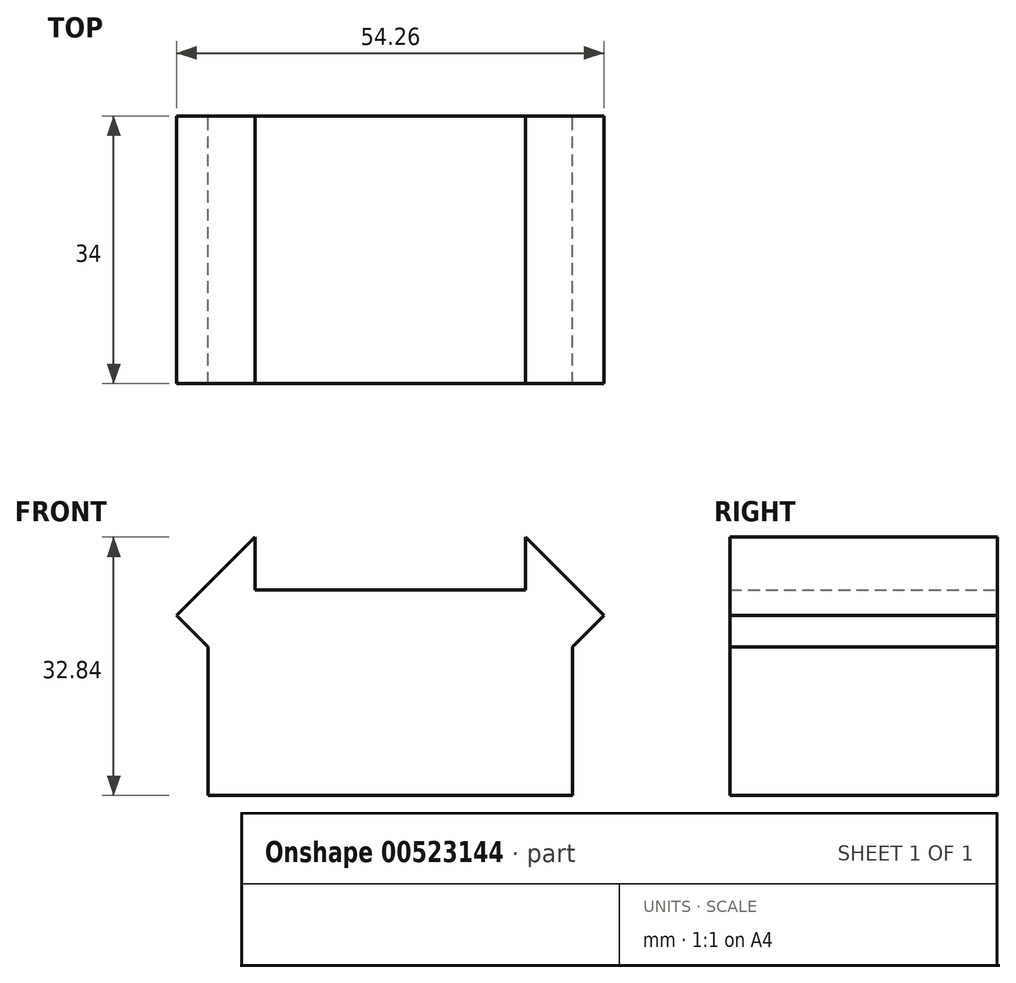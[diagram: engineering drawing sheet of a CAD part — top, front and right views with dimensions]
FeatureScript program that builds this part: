
annotation { "Feature Type Name" : "Feature", "Feature Type Description" : "" }
export const myFeature = defineFeature(function(context is Context, id is Id, definition is map)
    precondition{}
    {
        {
            var Q0;
            Q0=qCreatedBy(makeId("Front.planeOp"),FACE);
            var sketch = newSketch(context, id + "F0", { "sketchPlane" : qUnion([Q0])});
            skLineSegment(sketch, "E0", {"start": v(-23.15, -13.08) * mm, "end": v(23.15, -13.08) * mm});
            skLineSegment(sketch, "E1", {"start": v(23.15, -13.07) * mm, "end": v(23.15, 5.8) * mm});
            skLineSegment(sketch, "E2", {"start": v(23.15, 5.8) * mm, "end": v(27.13, 9.8) * mm});
            skLineSegment(sketch, "E3", {"start": v(27.13, 9.8) * mm, "end": v(17.15, 19.77) * mm});
            skLineSegment(sketch, "E4", {"start": v(17.15, 19.77) * mm, "end": v(17.15, 13.08) * mm});
            skLineSegment(sketch, "E5", {"start": v(17.15, 13.08) * mm, "end": v(-17.15, 13.07) * mm});
            skLineSegment(sketch, "E6", {"start": v(-17.15, 13.07) * mm, "end": v(-17.15, 19.77) * mm});
            skLineSegment(sketch, "E7", {"start": v(-17.15, 19.77) * mm, "end": v(-27.13, 9.8) * mm});
            skLineSegment(sketch, "E8", {"start": v(-27.13, 9.8) * mm, "end": v(-23.15, 5.8) * mm});
            skLineSegment(sketch, "E9", {"start": v(-23.15, 5.8) * mm, "end": v(-23.15, -13.08) * mm});
            skSolve(sketch);
        }
        {
            var Q0;
            Q0 = qSketchRegion(id + "F0", true);
            extrude(context, id + "F1", {"entities" : qUnion([Q0]), "depth" : 34 * mm, "offsetDistance" : 25 * mm});
        }
    });
